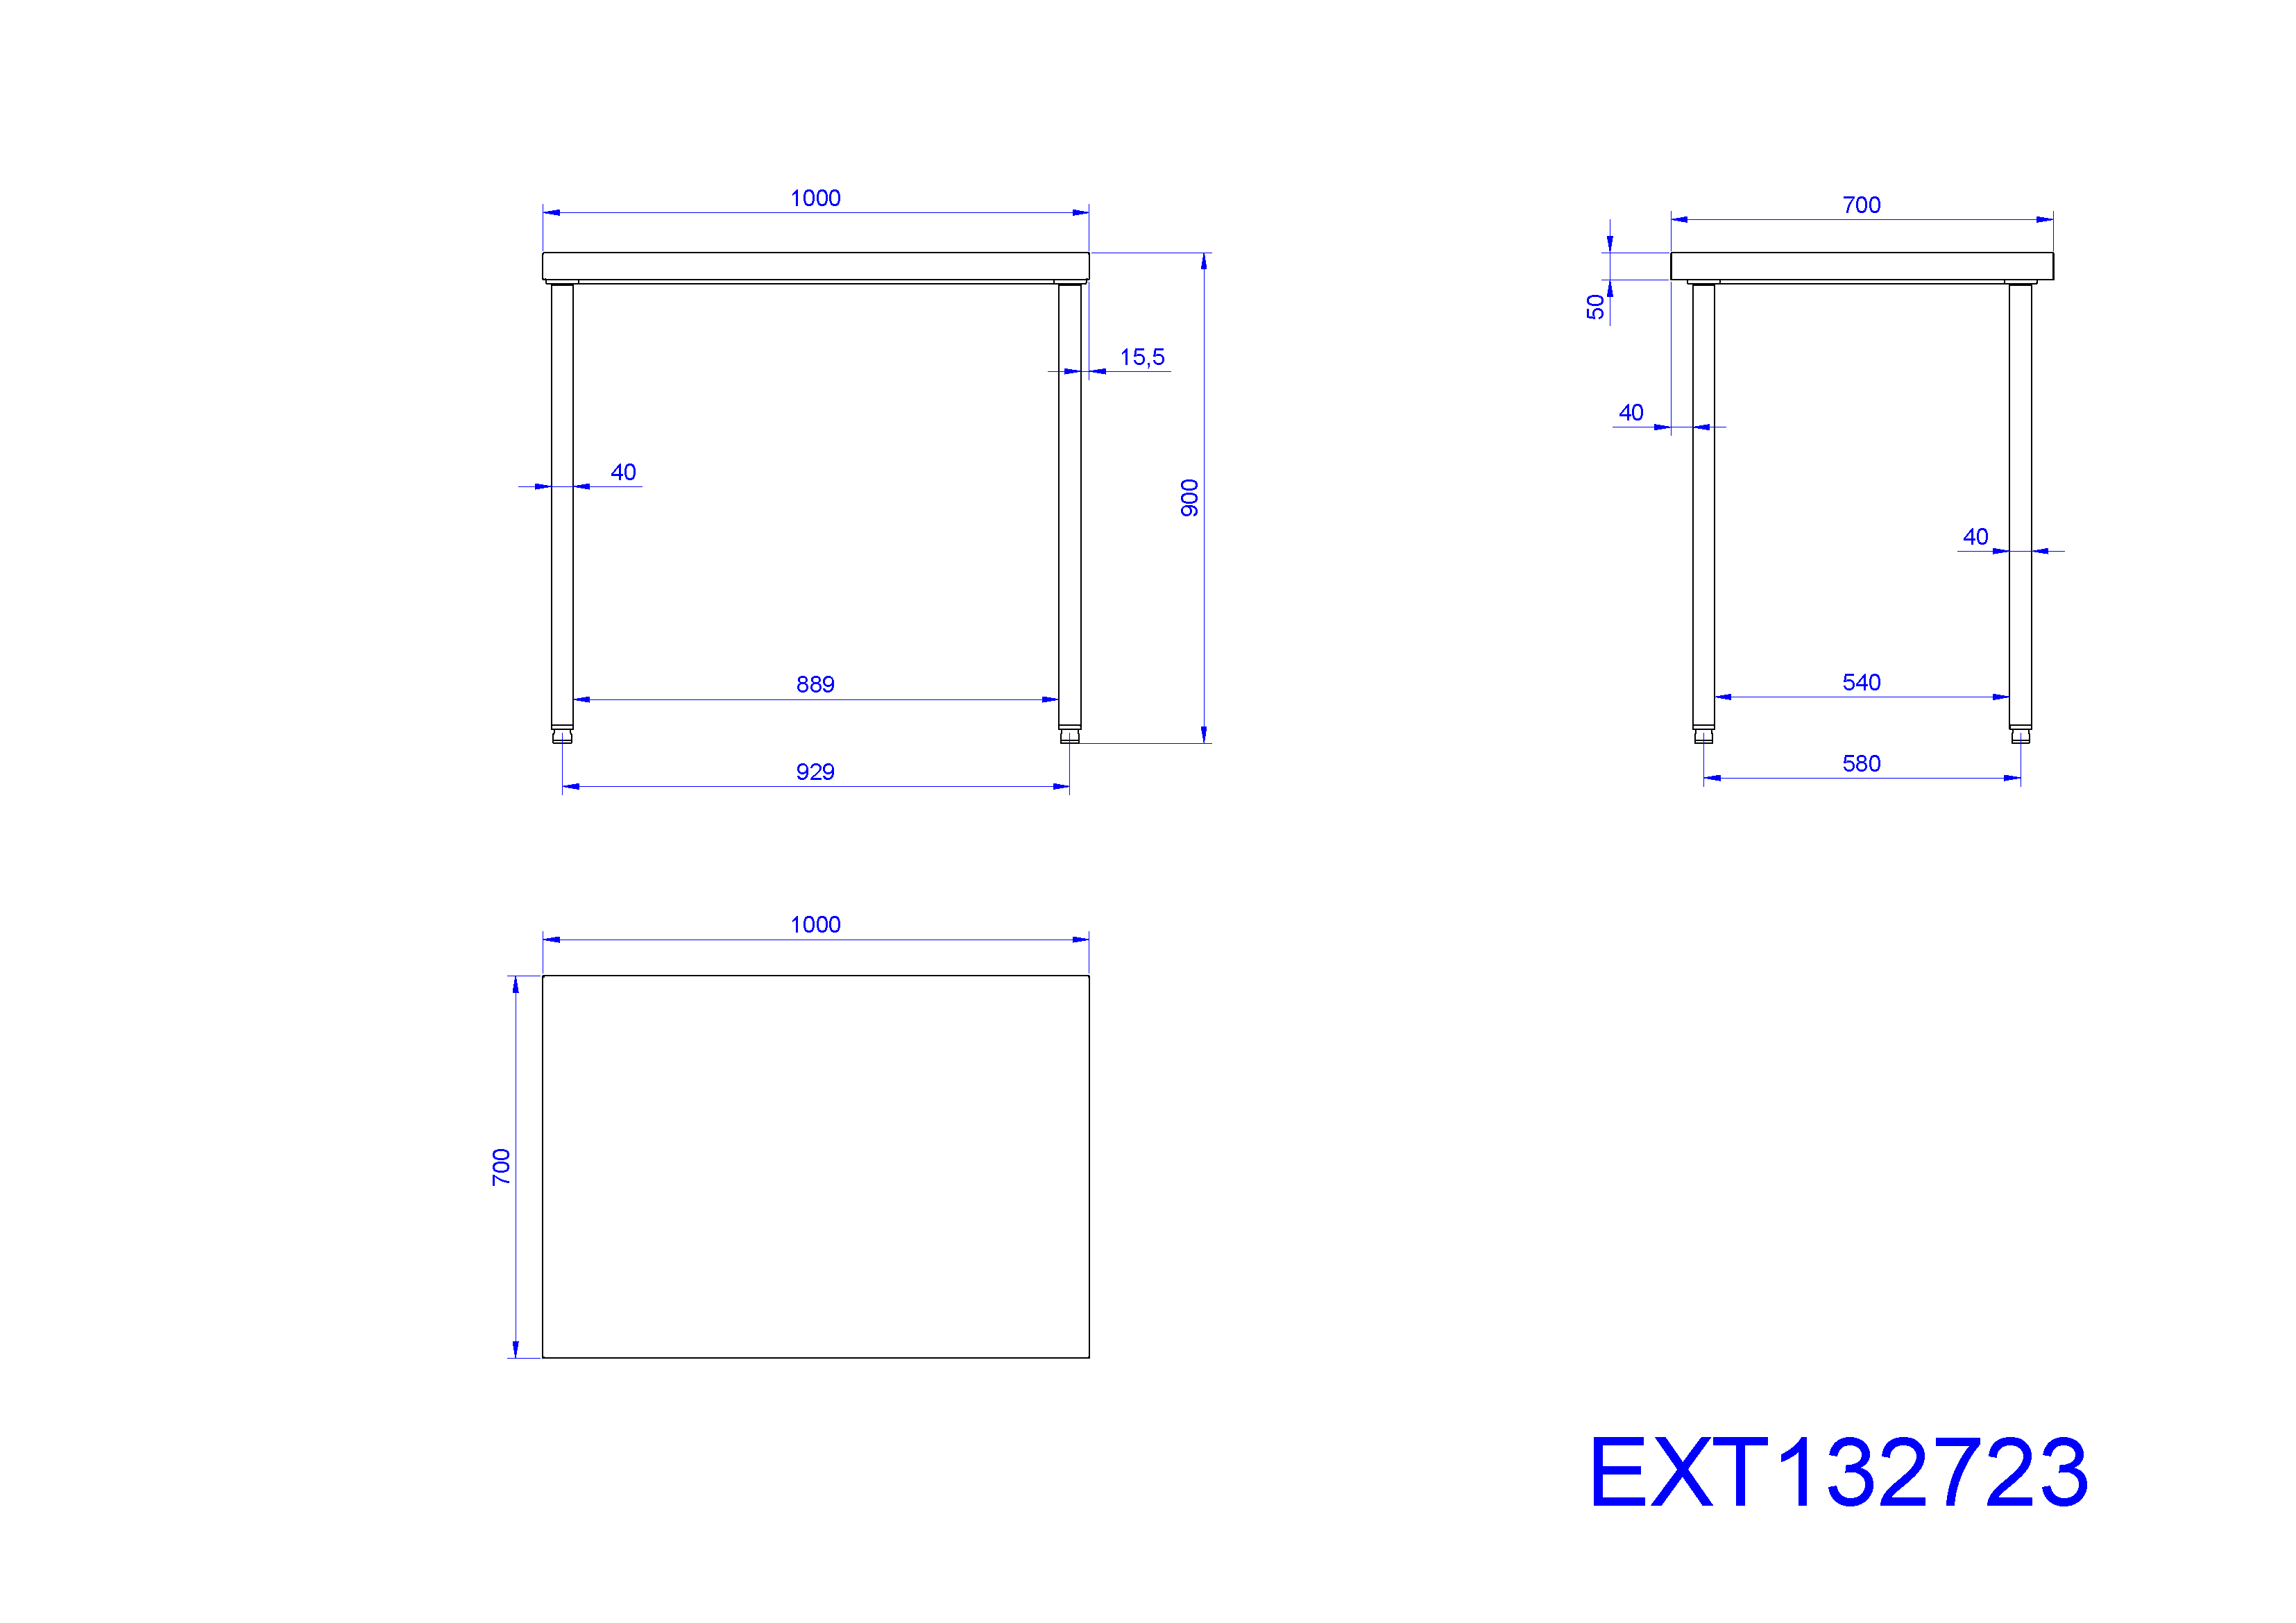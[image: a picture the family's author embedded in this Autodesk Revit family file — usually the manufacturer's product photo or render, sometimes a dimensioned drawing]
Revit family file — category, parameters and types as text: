
# Revit family: QF_ELECTROLUXPROFESSIONAL_133251_MLA1426PN
name_source: partatom
category: Attrezzature speciali
units: mm (PartAtom-declared; Revit-internal decimal feet)

## family parameters
Basato su piano di lavoro = No
Condiviso = No
Punto di calcolo locali = No
Quota connettore circolare = Usa diametro
Sempre verticale = Sì
Taglio con vuoti quando caricato = No
Tipo di parte = Normale

## types (1)
- Standard
    Accessory = Sì
    Cold Water Size = 0 mm
    Compressed Air Pressure = 0.0 Pa
    Compressed Air Size = 0 mm
    Compressed Air Volume = 0.0 L/s
    Condensate Return Size = 0 mm
    Cycle = 0 Hz
    Depth Actual = 700 mm  [stored 2.29659 ft]
    Descrizione = CUPBOARD SINK 2 BOWLS (600X500) 1400 MM
    Direct Waste Size = 51 mm
    Gas Input Pressure = 0
    Gas KW = 0
    Gas Size = 0 mm
    HP = 0 HP
    Height Actual = 1000 mm  [stored 3.28084 ft]
    Hot Water Size = 0 mm
    Item Number = 133251
    Length Actual = 1400 mm  [stored 4.59318 ft]
    Modello = MLA1426PN
    Phase = 0
    Produttore = Electrolux Professional
    Prospetto di default = 0 mm  [stored 0 ft]
    Refrigerant Compressor Remote = Sì
    Refrigeration Liquid Line Size = 0 mm  [stored 0 ft]
    Refrigeration Suction Line Size = 0 mm  [stored 0 ft]
    Steam Consumption per Hour = 0
    Steam Supply Maximum Pressure = 0.0 Pa
    Steam Supply Minimum Pressure = 0.0 Pa
    Steam Supply Size = 0 mm
    URL = https://www.electroluxprofessional.com
    URL Manufacturer = https://www.electroluxprofessional.com
    Volts = 0 V
    Watts = 0 W
    Weight = 60.00 kg

note: source unit labels omitted for Gas Input Pressure — the stored unit's dimension contradicts the parameter name (converter mislabeling)

note: [stored X ft] marks values corroborated as IEEE doubles in the binary element streams (Revit-internal decimal feet)

## geometry (parser evidence)
native form markers: Sweep x5
no freeform markers — native parametric forms only
